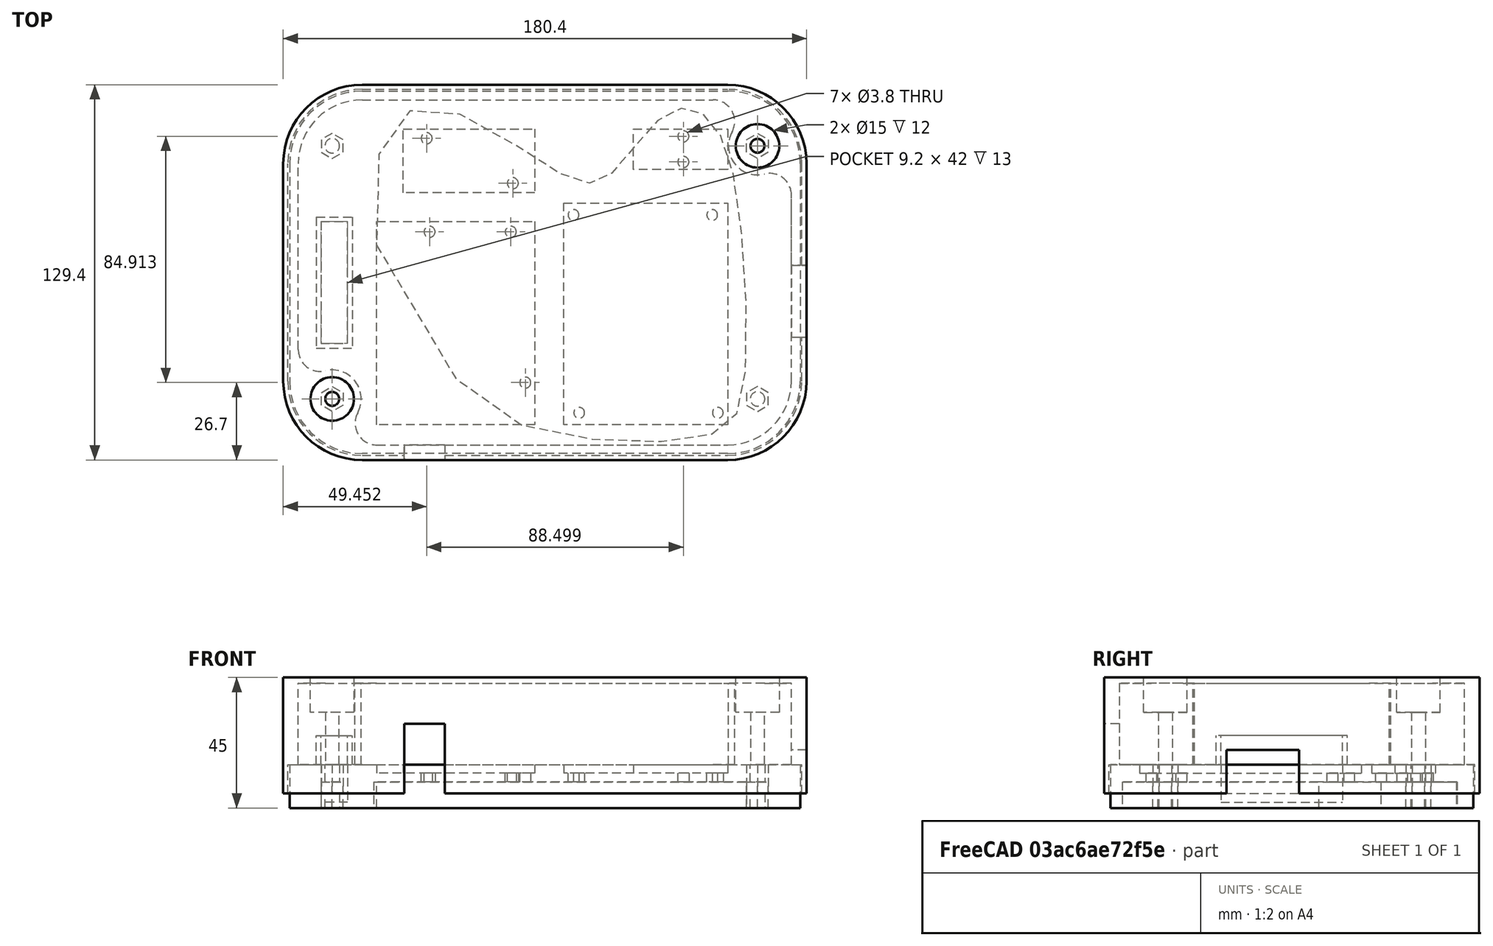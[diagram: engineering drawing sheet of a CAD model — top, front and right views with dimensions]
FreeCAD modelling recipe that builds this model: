
FCSTD DOCUMENT  (FreeCAD 0.21R33694 (Git))
Label: mers_door_controller
License: All rights reserved
LicenseURL: http://en.wikipedia.org/wiki/All_rights_reserved
objects: Sketcher::SketchObject×22, PartDesign::Pocket×17, PartDesign::Pad×5, PartDesign::Body×2, Mesh::Feature×2, PartDesign::Fillet×1, PartDesign::SubShapeBinder×1
note: 71 computed .brp shape members not serialized (recipe doc carries the construction recipe); baked Part::Feature solids carry a one-line shape summary decoded from their .brp

FEATURE [Sketcher::SketchObject] Sketch
  FullyConstrained = true
  MapMode = 5
  Support = -> [XY_Plane]
  sketch-geometry (4):
    g0: LineSegment StartX=-125 StartY=125 StartZ=0 EndX=125 EndY=125 EndZ=0
    g1: LineSegment StartX=125 StartY=125 StartZ=0 EndX=125 EndY=-125 EndZ=0
    g2: LineSegment StartX=125 StartY=-125 StartZ=0 EndX=-125 EndY=-125 EndZ=0
    g3: LineSegment StartX=-125 StartY=-125 StartZ=0 EndX=-125 EndY=125 EndZ=0
  constraints (11):
    c: Coincident(g0,g1)
    c: Coincident(g1,g2)
    c: Coincident(g2,g3)
    c: Coincident(g3,g0)
    c: Horizontal(g0)
    c: Horizontal(g2)
    c: Vertical(g1)
    c: Vertical(g3)
    c: Symmetric(g0,g2,g-1)
    c: Distance(g0) = 250
    c: Distance(g3) = 250
FEATURE [PartDesign::Pad] Pad
  Direction = (0,0,1)
  Length = 15
  Length2 = 10
  Profile = -> Sketch
  ReferenceAxis = -> Sketch [N_Axis]
  Type = 0
FEATURE [Sketcher::SketchObject] Sketch001
  ExternalGeometry = -> [Pad]
  FullyConstrained = true
  MapMode = 5
  Placement = pos=(0,0,15) rot=(0,0,1;0rad)
  Support = -> [Pad]
  sketch-geometry (16):
    g0: LineSegment StartX=-59.5 StartY=-45 StartZ=0 EndX=-5 EndY=-45 EndZ=0
    g1: LineSegment StartX=-5 StartY=-45 StartZ=0 EndX=-5 EndY=-115 EndZ=0
    g2: LineSegment StartX=-5 StartY=-115 StartZ=0 EndX=-59.5 EndY=-115 EndZ=0
    g3: LineSegment StartX=-59.5 StartY=-115 StartZ=0 EndX=-59.5 EndY=-45 EndZ=0
    g4: LineSegment StartX=5 StartY=-38.6 StartZ=0 EndX=61.5 EndY=-38.6 EndZ=0
    g5: LineSegment StartX=61.5 StartY=-38.6 StartZ=0 EndX=61.5 EndY=-115 EndZ=0
    g6: LineSegment StartX=61.5 StartY=-115 StartZ=0 EndX=5 EndY=-115 EndZ=0
    g7: LineSegment StartX=5 StartY=-115 StartZ=0 EndX=5 EndY=-38.6 EndZ=0
    g8: LineSegment StartX=-50.3 StartY=-13 StartZ=0 EndX=-5 EndY=-13 EndZ=0
    g9: LineSegment StartX=-5 StartY=-13 StartZ=0 EndX=-5 EndY=-35 EndZ=0
    g10: LineSegment StartX=-5 StartY=-35 StartZ=0 EndX=-50.3 EndY=-35 EndZ=0
    g11: LineSegment StartX=-50.3 StartY=-35 StartZ=0 EndX=-50.3 EndY=-13 EndZ=0
    g12: LineSegment StartX=29 StartY=-13 StartZ=0 EndX=61.5 EndY=-13 EndZ=0
    g13: LineSegment StartX=61.5 StartY=-13 StartZ=0 EndX=61.5 EndY=-27 EndZ=0
    g14: LineSegment StartX=61.5 StartY=-27 StartZ=0 EndX=29 EndY=-27 EndZ=0
    g15: LineSegment StartX=29 StartY=-27 StartZ=0 EndX=29 EndY=-13 EndZ=0
  constraints (47):
    c: Coincident(g0,g1)
    c: Coincident(g1,g2)
    c: Coincident(g2,g3)
    c: Coincident(g3,g0)
    c: Horizontal(g0)
    c: Horizontal(g2)
    c: Vertical(g1)
    c: Vertical(g3)
    c: Distance(g0) = 54.5
    c: Distance(g1) = 70
    c: Distance(g1,g-3) = 10
    c: Coincident(g4,g5)
    c: Coincident(g5,g6)
    c: Coincident(g6,g7)
    c: Coincident(g7,g4)
    c: Horizontal(g4)
    c: Horizontal(g6)
    c: Vertical(g5)
    c: Vertical(g7)
    c: Distance(g4) = 56.5
    c: Distance(g5) = 76.4
    c: DistanceX(g0,g4) = 10
    c: Coincident(g9,g10)
    c: Coincident(g10,g11)
    c: Coincident(g11,g8)
    c: Horizontal(g8)
    c: Horizontal(g10)
    c: Vertical(g9)
    c: Vertical(g11)
    c: Distance(g9) = 22
    c: Distance(g10) = 45.3
    c: PointOnObject(g9,g1)
    c: DistanceY(g0,g10) = 10
    c: Coincident(g12,g13)
    c: Coincident(g13,g14)
    c: Coincident(g14,g15)
    c: Coincident(g15,g12)
    c: Horizontal(g12)
    c: Horizontal(g14)
    c: Vertical(g13)
    c: Vertical(g15)
    c: Distance(g12) = 32.5
    c: Distance(g13) = 14
    c: PointOnObject(g13,g5)
    c: Coincident(g8,g9)
    c: PointOnObject(g12,g8)
    c: Symmetric(g1,g6,g-2)
FEATURE [PartDesign::Pocket] Pocket
  BaseFeature = -> Pad
  Direction = (0,0,-1)
  Length = 3
  Length2 = 5
  Profile = -> Sketch001
  ReferenceAxis = -> Sketch001 [N_Axis]
  Type = 0
FEATURE [Sketcher::SketchObject] Sketch002
  ExternalGeometry = -> [Pocket]
  FullyConstrained = true
  MapMode = 5
  Placement = pos=(0,0,12) rot=(0,0,1;0rad)
  Support = -> [Pocket]
  expr: Constraints[4] = 51 - 3.2
  expr: Constraints[5] = 71.45 - 3.2
  sketch-geometry (7):
    g0: Circle CenterX=8.37519 CenterY=-42.6889 CenterZ=0 NormalX=0 NormalY=0 NormalZ=1 AngleXU=0 Radius=1.85
    g1: Circle CenterX=56.1752 CenterY=-42.6889 CenterZ=0 NormalX=0 NormalY=0 NormalZ=1 AngleXU=0 Radius=1.85
    g2: Circle CenterX=58.1248 CenterY=-110.911 CenterZ=0 NormalX=0 NormalY=0 NormalZ=1 AngleXU=0 Radius=1.85
    g3: Circle CenterX=10.3248 CenterY=-110.911 CenterZ=0 NormalX=0 NormalY=0 NormalZ=1 AngleXU=0 Radius=1.85
    g4: LineSegment StartX=61.5 StartY=-38.6 StartZ=0 EndX=5 EndY=-115 EndZ=0
    g5: LineSegment StartX=5 StartY=-38.6 StartZ=0 EndX=61.5 EndY=-115 EndZ=0
    g6: GeomPoint X=33.25 Y=-76.8 Z=0
  constraints (16):
    c: Equal(g1,g0)
    c: Equal(g0,g3)
    c: Equal(g3,g2)
    c: Diameter(g1) = 3.7
    c: Distance(g0,g1) = 47.8
    c: Distance(g1,g2) = 68.25
    c: Coincident(g4,g-5)
    c: Coincident(g4,g-6)
    c: Tangent(g4,g1)
    c: Coincident(g5,g-4)
    c: Coincident(g5,g-6)
    c: PointOnObject(g6,g5)
    c: PointOnObject(g6,g4)
    c: Symmetric(g1,g3,g6)
    c: Symmetric(g0,g2,g6)
    c: Horizontal(g3,g2)
FEATURE [PartDesign::Pocket] Pocket001
  BaseFeature = -> Pocket
  Direction = (0,0,-1)
  Length = 5
  Length2 = 5
  Profile = -> Sketch002
  ReferenceAxis = -> Sketch002 [N_Axis]
  Type = 1
FEATURE [Sketcher::SketchObject] Sketch003
  ExternalGeometry = -> [Pocket001]
  FullyConstrained = true
  MapMode = 5
  Placement = pos=(0,0,12) rot=(0,0,1;0rad)
  Support = -> [Pocket001]
  expr: Constraints[21] = 1 + 3.8 / 2
  expr: Constraints[22] = 1 + 3.8 / 2
  expr: Constraints[23] = 12 + 3.8 / 2
  expr: Constraints[24] = 6 + 3.8 / 2
  expr: Constraints[3] = 31.8 - 3.8
  sketch-geometry (10):
    g0: Circle CenterX=-41.25 CenterY=-48.5 CenterZ=0 NormalX=0 NormalY=0 NormalZ=1 AngleXU=0 Radius=1.9
    g1: Circle CenterX=-13.25 CenterY=-48.5 CenterZ=0 NormalX=0 NormalY=0 NormalZ=1 AngleXU=0 Radius=1.9
    g2: Circle CenterX=-8.25 CenterY=-100.5 CenterZ=0 NormalX=0 NormalY=0 NormalZ=1 AngleXU=0 Radius=1.9
    g3: LineSegment StartX=-59.15 StartY=-45.6 StartZ=0 EndX=-5.35 EndY=-45.6 EndZ=0
    g4: LineSegment StartX=-5.35 StartY=-45.6 StartZ=0 EndX=-5.35 EndY=-114.4 EndZ=0
    g5: LineSegment StartX=-5.35 StartY=-114.4 StartZ=0 EndX=-59.15 EndY=-114.4 EndZ=0
    g6: LineSegment StartX=-59.15 StartY=-114.4 StartZ=0 EndX=-59.15 EndY=-45.6 EndZ=0
    g7: LineSegment StartX=-5 StartY=-45 StartZ=0 EndX=-59.5 EndY=-115 EndZ=0
    g8: LineSegment StartX=-5 StartY=-115 StartZ=0 EndX=-59.5 EndY=-45 EndZ=0
    g9: GeomPoint X=-32.25 Y=-80 Z=0
  constraints (25):
    c: Equal(g1,g2)
    c: Equal(g2,g0)
    c: Diameter(g0) = 3.8
    c: Distance(g0,g1) = 28
    c: Horizontal(g0,g1)
    c: Coincident(g3,g4)
    c: Coincident(g4,g5)
    c: Coincident(g5,g6)
    c: Coincident(g6,g3)
    c: Horizontal(g3)
    c: Vertical(g4)
    c: Coincident(g7,g-5)
    c: Coincident(g7,g-6)
    c: Coincident(g8,g-5)
    c: Coincident(g8,g-6)
    c: PointOnObject(g9,g7)
    c: PointOnObject(g9,g8)
    c: Symmetric(g5,g3,g9)
    c: Symmetric(g3,g4,g9)
    c: Distance(g5) = 53.8
    c: Distance(g6) = 68.8
    c: Distance(g1,g3) = 2.9
    c: Distance(g2,g4) = 2.9
    c: Distance(g2,g5) = 13.9
    c: Distance(g1,g4) = 7.9
FEATURE [PartDesign::Pocket] Pocket002
  BaseFeature = -> Pocket001
  Direction = (0,0,-1)
  Length = 5
  Length2 = 5
  Profile = -> Sketch003
  ReferenceAxis = -> Sketch003 [N_Axis]
  Type = 1
FEATURE [Sketcher::SketchObject] Sketch004
  ExternalGeometry = -> [Pocket002]
  FullyConstrained = true
  MapMode = 5
  Placement = pos=(0,0,12) rot=(0,0,1;0rad)
  Support = -> [Pocket002]
  expr: Constraints[19] = 37 - 3.5
  expr: Constraints[20] = 1 + 3.5 / 2
  expr: Constraints[21] = 5.3 + 3.5 / 2
  expr: Constraints[22] = 1 + 3.5 / 2
  sketch-geometry (9):
    g0: Circle CenterX=-42.2485 CenterY=-16.25 CenterZ=0 NormalX=0 NormalY=0 NormalZ=1 AngleXU=0 Radius=1.9
    g1: Circle CenterX=-12.55 CenterY=-31.75 CenterZ=0 NormalX=0 NormalY=0 NormalZ=1 AngleXU=0 Radius=1.9
    g2: LineSegment StartX=-50.3 StartY=-35 StartZ=0 EndX=-5 EndY=-13 EndZ=0
    g3: LineSegment StartX=-50.3 StartY=-13 StartZ=0 EndX=-5 EndY=-35 EndZ=0
    g4: GeomPoint X=-27.65 Y=-24 Z=0
    g5: LineSegment StartX=-49.8 StartY=-13.5 StartZ=0 EndX=-5.5 EndY=-13.5 EndZ=0
    g6: LineSegment StartX=-5.5 StartY=-13.5 StartZ=0 EndX=-5.5 EndY=-34.5 EndZ=0
    g7: LineSegment StartX=-5.5 StartY=-34.5 StartZ=0 EndX=-49.8 EndY=-34.5 EndZ=0
    g8: LineSegment StartX=-49.8 StartY=-34.5 StartZ=0 EndX=-49.8 EndY=-13.5 EndZ=0
  constraints (23):
    c: Equal(g1,g0)
    c: Diameter(g0) = 3.8
    c: Coincident(g2,g-6)
    c: Coincident(g2,g-4)
    c: Coincident(g3,g-6)
    c: Coincident(g3,g-5)
    c: PointOnObject(g4,g2)
    c: PointOnObject(g4,g3)
    c: Coincident(g5,g6)
    c: Coincident(g6,g7)
    c: Coincident(g7,g8)
    c: Coincident(g8,g5)
    c: Horizontal(g5)
    c: Horizontal(g7)
    c: Vertical(g6)
    c: Vertical(g8)
    c: Distance(g6) = 21
    c: Distance(g7) = 44.3
    c: Symmetric(g7,g5,g4)
    c: Distance(g0,g1) = 33.5
    c: Distance(g1,g7) = 2.75
    c: Distance(g1,g6) = 7.05
    c: Distance(g0,g5) = 2.75
FEATURE [PartDesign::Pocket] Pocket003
  BaseFeature = -> Pocket002
  Direction = (0,0,-1)
  Length = 5
  Length2 = 5
  Profile = -> Sketch004
  ReferenceAxis = -> Sketch004 [N_Axis]
  Type = 1
FEATURE [Sketcher::SketchObject] Sketch005
  ExternalGeometry = -> [Pocket003]
  FullyConstrained = true
  MapMode = 5
  Placement = pos=(0,0,12) rot=(0,0,1;0rad)
  Support = -> [Pocket003]
  expr: Constraints[21] = 13 + 3.5 / 2
  sketch-geometry (11):
    g0: LineSegment StartX=61.5 StartY=-13 StartZ=0 EndX=29 EndY=-27 EndZ=0
    g1: LineSegment StartX=29 StartY=-13 StartZ=0 EndX=61.5 EndY=-27 EndZ=0
    g2: GeomPoint X=45.25 Y=-20 Z=0
    g3: LineSegment StartX=29.5 StartY=-13.5 StartZ=0 EndX=61 EndY=-13.5 EndZ=0
    g4: LineSegment StartX=61 StartY=-13.5 StartZ=0 EndX=61 EndY=-26.5 EndZ=0
    g5: LineSegment StartX=61 StartY=-26.5 StartZ=0 EndX=29.5 EndY=-26.5 EndZ=0
    g6: LineSegment StartX=29.5 StartY=-26.5 StartZ=0 EndX=29.5 EndY=-13.5 EndZ=0
    g7: Circle CenterX=46.25 CenterY=-15.5869 CenterZ=0 NormalX=0 NormalY=0 NormalZ=1 AngleXU=0 Radius=1.9
    g8: Circle CenterX=46.25 CenterY=-24.4131 CenterZ=0 NormalX=0 NormalY=0 NormalZ=1 AngleXU=0 Radius=1.9
    g9: LineSegment StartX=46.25 StartY=-15.5869 StartZ=0 EndX=45.25 EndY=-20 EndZ=0
    g10: LineSegment StartX=46.25 StartY=-24.4131 StartZ=0 EndX=45.25 EndY=-20 EndZ=0
  constraints (27):
    c: Coincident(g0,g-6)
    c: Coincident(g0,g-5)
    c: Coincident(g1,g-5)
    c: Coincident(g1,g-6)
    c: PointOnObject(g2,g0)
    c: PointOnObject(g2,g1)
    c: Coincident(g3,g4)
    c: Coincident(g4,g5)
    c: Coincident(g5,g6)
    c: Coincident(g6,g3)
    c: Horizontal(g3)
    c: Horizontal(g5)
    c: Vertical(g4)
    c: Vertical(g6)
    c: Distance(g4) = 13
    c: Distance(g5) = 31.5
    c: Symmetric(g5,g3,g2)
    c: Equal(g8,g7)
    c: Diameter(g7) = 3.8
    c: Distance(g7,g8) = 8.82622
    c: Vertical(g7,g8)
    c: Distance(g8,g4) = 14.75
    c: Coincident(g9,g7)
    c: Coincident(g9,g2)
    c: Coincident(g10,g8)
    c: Coincident(g10,g2)
    c: Equal(g10,g9)
FEATURE [PartDesign::Pocket] Pocket004
  BaseFeature = -> Pocket003
  Direction = (0,0,-1)
  Length = 5
  Length2 = 5
  Profile = -> Sketch005
  ReferenceAxis = -> Sketch005 [N_Axis]
  Type = 1
FEATURE [Sketcher::SketchObject] Sketch006
  ExternalGeometry = -> [Pocket004]
  FullyConstrained = true
  MapMode = 5
  Placement = pos=(0,0,15) rot=(0,0,1;0rad)
  Support = -> [Pocket004]
  sketch-geometry (4):
    g0: LineSegment StartX=-78.7 StartY=-45 StartZ=0 EndX=-69.5 EndY=-45 EndZ=0
    g1: LineSegment StartX=-69.5 StartY=-45 StartZ=0 EndX=-69.5 EndY=-87 EndZ=0
    g2: LineSegment StartX=-69.5 StartY=-87 StartZ=0 EndX=-78.7 EndY=-87 EndZ=0
    g3: LineSegment StartX=-78.7 StartY=-87 StartZ=0 EndX=-78.7 EndY=-45 EndZ=0
  constraints (12):
    c: Coincident(g0,g1)
    c: Coincident(g1,g2)
    c: Coincident(g2,g3)
    c: Coincident(g3,g0)
    c: Horizontal(g0)
    c: Horizontal(g2)
    c: Vertical(g1)
    c: Vertical(g3)
    c: Distance(g0) = 9.2
    c: Distance(g1) = 42
    c: Distance(g0,g-3) = 10
    c: PointOnObject(g0,g-4)
FEATURE [PartDesign::Pocket] Pocket005
  BaseFeature = -> Pocket004
  Direction = (0,0,-1)
  Length = 13
  Length2 = 5
  Profile = -> Sketch006
  ReferenceAxis = -> Sketch006 [N_Axis]
  Type = 0
FEATURE [Sketcher::SketchObject] Sketch007
  ExternalGeometry = -> [Pocket005]
  FullyConstrained = true
  MapMode = 5
  Placement = pos=(0,0,15) rot=(0,0,1;0rad)
  Support = -> [Pocket005]
  sketch-geometry (11):
    g0: LineSegment StartX=-78.7 StartY=-45 StartZ=0 EndX=-78.7 EndY=-87 EndZ=0
    g1: LineSegment StartX=-69.5 StartY=-87 StartZ=0 EndX=-69.5 EndY=-45 EndZ=0
    g2: LineSegment StartX=-78.7 StartY=-87 StartZ=0 EndX=-69.5 EndY=-87 EndZ=0
    g3: LineSegment StartX=-78.7 StartY=-45 StartZ=0 EndX=-69.5 EndY=-45 EndZ=0
    g4: LineSegment StartX=-80.3 StartY=-43.4 StartZ=0 EndX=-67.9 EndY=-43.4 EndZ=0
    g5: LineSegment StartX=-67.9 StartY=-43.4 StartZ=0 EndX=-67.9 EndY=-88.6 EndZ=0
    g6: LineSegment StartX=-80.3 StartY=-88.6 StartZ=0 EndX=-67.9 EndY=-88.6 EndZ=0
    g7: LineSegment StartX=-80.3 StartY=-43.4 StartZ=0 EndX=-80.3 EndY=-88.6 EndZ=0
    g8: LineSegment StartX=-69.5 StartY=-45 StartZ=0 EndX=-78.7 EndY=-87 EndZ=0
    g9: LineSegment StartX=-78.7 StartY=-45 StartZ=0 EndX=-69.5 EndY=-87 EndZ=0
    g10: GeomPoint X=-74.1 Y=-66 Z=0
  constraints (24):
    c: Coincident(g3,g1)
    c: Coincident(g0,g3)
    c: Coincident(g0,g2)
    c: Coincident(g2,g1)
    c: Coincident(g1,g-6)
    c: Coincident(g0,g-6)
    c: Coincident(g-4,g1)
    c: Coincident(g0,g-5)
    c: Coincident(g4,g5)
    c: Coincident(g7,g4)
    c: Coincident(g7,g6)
    c: Coincident(g6,g5)
    c: Coincident(g8,g1)
    c: Coincident(g8,g0)
    c: Coincident(g9,g0)
    c: Coincident(g9,g1)
    c: PointOnObject(g10,g8)
    c: PointOnObject(g10,g9)
    c: Symmetric(g6,g4,g10)
    c: Symmetric(g5,g4,g10)
    c: Parallel(g1,g5)
    c: Parallel(g3,g4)
    c: Distance(g1,g5) = 1.6
    c: Distance(g1,g4) = 1.6
FEATURE [PartDesign::Pad] Pad001
  BaseFeature = -> Pocket005
  Direction = (0,0,1)
  Length = 10
  Length2 = 10
  Profile = -> Sketch007
  ReferenceAxis = -> Sketch007 [N_Axis]
  Type = 0
FEATURE [Sketcher::SketchObject] Sketch008
  ExternalGeometry = -> [Pad001]
  FullyConstrained = true
  MapMode = 5
  Placement = pos=(0,0,15) rot=(0,0,1;0rad)
  Support = -> [Pad001]
  sketch-geometry (12):
    g0: Circle CenterX=71.5 CenterY=-15 CenterZ=0 NormalX=0 NormalY=0 NormalZ=1 AngleXU=0 Radius=15
    g1: Circle CenterX=71.5 CenterY=-110 CenterZ=0 NormalX=0 NormalY=0 NormalZ=1 AngleXU=0 Radius=15
    g2: Circle CenterX=-74.5 CenterY=-15 CenterZ=0 NormalX=0 NormalY=0 NormalZ=1 AngleXU=0 Radius=15
    g3: Circle CenterX=-74.5 CenterY=-110 CenterZ=0 NormalX=0 NormalY=0 NormalZ=1 AngleXU=0 Radius=15
    g4: LineSegment StartX=-89.5 StartY=-125 StartZ=0 EndX=86.5 EndY=-125 EndZ=0
    g5: LineSegment StartX=86.5 StartY=0 StartZ=0 EndX=86.5 EndY=-125 EndZ=0
    g6: LineSegment StartX=-89.5 StartY=0 StartZ=0 EndX=86.5 EndY=0 EndZ=0
    g7: LineSegment StartX=-89.5 StartY=0 StartZ=0 EndX=-89.5 EndY=-125 EndZ=0
    g8: LineSegment StartX=-150 StartY=150 StartZ=0 EndX=150 EndY=150 EndZ=0
    g9: LineSegment StartX=150 StartY=150 StartZ=0 EndX=150 EndY=-150 EndZ=0
    g10: LineSegment StartX=150 StartY=-150 StartZ=0 EndX=-150 EndY=-150 EndZ=0
    g11: LineSegment StartX=-150 StartY=-150 StartZ=0 EndX=-150 EndY=150 EndZ=0
  constraints (35):
    c: Equal(g0,g1)
    c: Equal(g1,g3)
    c: Equal(g3,g2)
    c: Diameter(g2) = 30
    c: Tangent(g3,g-4)
    c: Tangent(g1,g-4)
    c: Tangent(g0,g-1)
    c: Tangent(g2,g-1)
    c: Vertical(g1,g0)
    c: Vertical(g2,g3)
    c: Distance(g1,g-6) = 10
    c: Tangent(g3,g-7)
    c: Coincident(g7,g6)
    c: Coincident(g6,g5)
    c: Coincident(g4,g5)
    c: Coincident(g4,g7)
    c: PointOnObject(g5,g-1)
    c: PointOnObject(g6,g-1)
    c: PointOnObject(g4,g-4)
    c: PointOnObject(g4,g-4)
    c: Tangent(g0,g5)
    c: Tangent(g1,g5)
    c: Tangent(g7,g3)
    c: Tangent(g2,g7)
    c: Coincident(g8,g9)
    c: Coincident(g9,g10)
    c: Coincident(g10,g11)
    c: Coincident(g11,g8)
    c: Horizontal(g8)
    c: Horizontal(g10)
    c: Vertical(g9)
    c: Vertical(g11)
    c: Symmetric(g10,g8,g-1)
    c: Distance(g9) = 300
    c: Distance(g8) = 300
FEATURE [PartDesign::Pocket] Pocket006
  BaseFeature = -> Pad001
  Direction = (0,0,-1)
  Length = 5
  Length2 = 5
  Profile = -> Sketch008
  ReferenceAxis = -> Sketch008 [N_Axis]
  Type = 1
FEATURE [PartDesign::Fillet] Fillet
  Base = -> Pocket006 [Edge18,Edge20,Edge17,Edge22]
  BaseFeature = -> Pocket006
  Radius = 25
  SupportTransform = false
  UseAllEdges = false
FEATURE [Sketcher::SketchObject] Sketch009
  ExternalGeometry = -> [Fillet]
  FullyConstrained = true
  MapMode = 5
  Placement = pos=(0,0,15) rot=(0,0,1;0rad)
  Support = -> [Fillet]
  sketch-geometry (7):
    g0: Circle CenterX=-74.8115 CenterY=-18.8622 CenterZ=0 NormalX=0 NormalY=0 NormalZ=1 AngleXU=0 Radius=2.5
    g1: Circle CenterX=-74.8115 CenterY=-106.138 CenterZ=0 NormalX=0 NormalY=0 NormalZ=1 AngleXU=0 Radius=2.5
    g2: Circle CenterX=71.8115 CenterY=-106.138 CenterZ=0 NormalX=0 NormalY=0 NormalZ=1 AngleXU=0 Radius=2.5
    g3: Circle CenterX=71.8115 CenterY=-18.8622 CenterZ=0 NormalX=0 NormalY=0 NormalZ=1 AngleXU=0 Radius=2.5
    g4: LineSegment StartX=-64.5 StartY=-100 StartZ=0 EndX=61.5 EndY=-25 EndZ=0
    g5: LineSegment StartX=61.5 StartY=-100 StartZ=0 EndX=-64.5 EndY=-25 EndZ=0
    g6: GeomPoint X=-1.5 Y=-62.5 Z=0
  constraints (16):
    c: Equal(g0,g3)
    c: Equal(g3,g2)
    c: Equal(g2,g1)
    c: Diameter(g0) = 5
    c: Coincident(g4,g-5)
    c: Coincident(g4,g-3)
    c: Coincident(g5,g-4)
    c: Coincident(g5,g-6)
    c: PointOnObject(g6,g5)
    c: PointOnObject(g6,g4)
    c: Symmetric(g2,g0,g6)
    c: Symmetric(g1,g3,g6)
    c: Distance(g4,g3) = 12
    c: Distance(g5,g2) = 12
    c: PointOnObject(g2,g5)
    c: PointOnObject(g1,g4)
FEATURE [PartDesign::Pocket] Pocket007
  BaseFeature = -> Fillet
  Direction = (0,0,-1)
  Length = 5
  Length2 = 5
  Profile = -> Sketch009
  ReferenceAxis = -> Sketch009 [N_Axis]
  Type = 1
FEATURE [Sketcher::SketchObject] Sketch010
  FullyConstrained = false
  MapMode = 5
  Placement = pos=(0,0,0) rot=(1,0,0;3.14159rad)
  Support = -> [Pocket007]
  sketch-geometry (25):
    g0-g12: Circle x13 (B-spline internal-alignment scaffolding for g13; pole/knot coordinates omitted)
    g13: BSplineCurve PolesCount=13 KnotsCount=11 Degree=3 IsPeriodic=0
    g14-g24: GeomPoint x11 (B-spline internal-alignment scaffolding for g13; pole/knot coordinates omitted)
  constraints (5):
    c: Weight(g0) = 1
    c: Equal(g0, g1-g12) x12
    c: Coincident(g13,g0)
    c: InternalAlignment(g0-g12 -> g13) x13
    c: InternalAlignment(g14-g24 -> g13) x11
FEATURE [PartDesign::Pocket] Pocket008
  BaseFeature = -> Pocket007
  Direction = (0,0,1)
  Length = 9
  Length2 = 5
  Profile = -> Sketch010
  ReferenceAxis = -> Sketch010 [N_Axis]
  Type = 0
FEATURE [Sketcher::SketchObject] Sketch011
  ExternalGeometry = -> [Pocket008]
  FullyConstrained = true
  MapMode = 5
  Placement = pos=(0,0,15) rot=(0,0,1;0rad)
  Support = -> [Pocket008]
  sketch-geometry (14):
    g0: LineSegment StartX=-71.0615 StartY=-21.0273 StartZ=0 EndX=-71.0615 EndY=-16.6971 EndZ=0
    g1: LineSegment StartX=-71.0615 StartY=-16.6971 StartZ=0 EndX=-74.8115 EndY=-14.5321 EndZ=0
    g2: LineSegment StartX=-74.8115 StartY=-14.5321 StartZ=0 EndX=-78.5615 EndY=-16.6971 EndZ=0
    g3: LineSegment StartX=-78.5615 StartY=-16.6971 StartZ=0 EndX=-78.5615 EndY=-21.0273 EndZ=0
    g4: LineSegment StartX=-78.5615 StartY=-21.0273 StartZ=0 EndX=-74.8115 EndY=-23.1923 EndZ=0
    g5: LineSegment StartX=-74.8115 StartY=-23.1923 StartZ=0 EndX=-71.0615 EndY=-21.0273 EndZ=0
    g6: Circle CenterX=-74.8115 CenterY=-18.8622 CenterZ=0 NormalX=0 NormalY=0 NormalZ=1 AngleXU=0 Radius=4.33013
    g7: LineSegment StartX=75.5615 StartY=-108.303 StartZ=0 EndX=75.5615 EndY=-103.973 EndZ=0
    g8: LineSegment StartX=75.5615 StartY=-103.973 StartZ=0 EndX=71.8115 EndY=-101.808 EndZ=0
    g9: LineSegment StartX=71.8115 StartY=-101.808 StartZ=0 EndX=68.0615 EndY=-103.973 EndZ=0
    g10: LineSegment StartX=68.0615 StartY=-103.973 StartZ=0 EndX=68.0615 EndY=-108.303 EndZ=0
    g11: LineSegment StartX=68.0615 StartY=-108.303 StartZ=0 EndX=71.8115 EndY=-110.468 EndZ=0
    g12: LineSegment StartX=71.8115 StartY=-110.468 StartZ=0 EndX=75.5615 EndY=-108.303 EndZ=0
    g13: Circle CenterX=71.8115 CenterY=-106.138 CenterZ=0 NormalX=0 NormalY=0 NormalZ=1 AngleXU=0 Radius=4.33013
  constraints (32):
    c: Coincident(g0,g1)
    c: Coincident(g1,g2)
    c: Coincident(g2,g3)
    c: Coincident(g3,g4)
    c: Coincident(g4,g5)
    c: Coincident(g5,g0)
    c: Equal(g0, g1-g5) x5
    c: PointOnObject(g0,g6)
    c: PointOnObject(g1,g6)
    c: PointOnObject(g2,g6)
    c: PointOnObject(g3,g6)
    c: PointOnObject(g4,g6)
    c: PointOnObject(g5,g6)
    c: Coincident(g7,g8)
    c: Coincident(g8,g9)
    c: Coincident(g9,g10)
    c: Coincident(g10,g11)
    c: Coincident(g11,g12)
    c: Coincident(g12,g7)
    c: Equal(g7, g8-g12) x5
    c: PointOnObject(g7,g13)
    c: PointOnObject(g8,g13)
    c: PointOnObject(g9,g13)
    c: PointOnObject(g10,g13)
    c: PointOnObject(g11,g13)
    c: PointOnObject(g12,g13)
    c: Equal(g13,g6)
    c: Distance(g4,g0) = 7.5
    c: Coincident(g6,g-3)
    c: Coincident(g-4,g13)
    c: Vertical(g7)
    c: Vertical(g0)
FEATURE [PartDesign::Pocket] Pocket009
  BaseFeature = -> Pocket008
  Direction = (0,0,-1)
  Length = 10
  Length2 = 5
  Profile = -> Sketch011
  ReferenceAxis = -> Sketch011 [N_Axis]
  Type = 0
FEATURE [Sketcher::SketchObject] Sketch012
  ExternalGeometry = -> [Pocket009]
  FullyConstrained = true
  MapMode = 5
  Placement = pos=(0,0,0) rot=(1,0,0;3.14159rad)
  Support = -> [Pocket009]
  sketch-geometry (14):
    g0: LineSegment StartX=-71.0615 StartY=103.973 StartZ=0 EndX=-71.0615 EndY=108.303 EndZ=0
    g1: LineSegment StartX=-71.0615 StartY=108.303 StartZ=0 EndX=-74.8115 EndY=110.468 EndZ=0
    g2: LineSegment StartX=-74.8115 StartY=110.468 StartZ=0 EndX=-78.5615 EndY=108.303 EndZ=0
    g3: LineSegment StartX=-78.5615 StartY=108.303 StartZ=0 EndX=-78.5615 EndY=103.973 EndZ=0
    g4: LineSegment StartX=-78.5615 StartY=103.973 StartZ=0 EndX=-74.8115 EndY=101.808 EndZ=0
    g5: LineSegment StartX=-74.8115 StartY=101.808 StartZ=0 EndX=-71.0615 EndY=103.973 EndZ=0
    g6: Circle CenterX=-74.8115 CenterY=106.138 CenterZ=0 NormalX=0 NormalY=0 NormalZ=1 AngleXU=0 Radius=4.33013
    g7: LineSegment StartX=75.5615 StartY=16.6971 StartZ=0 EndX=75.5615 EndY=21.0273 EndZ=0
    g8: LineSegment StartX=75.5615 StartY=21.0273 StartZ=0 EndX=71.8115 EndY=23.1923 EndZ=0
    g9: LineSegment StartX=71.8115 StartY=23.1923 StartZ=0 EndX=68.0615 EndY=21.0273 EndZ=0
    g10: LineSegment StartX=68.0615 StartY=21.0273 StartZ=0 EndX=68.0615 EndY=16.6971 EndZ=0
    g11: LineSegment StartX=68.0615 StartY=16.6971 StartZ=0 EndX=71.8115 EndY=14.5321 EndZ=0
    g12: LineSegment StartX=71.8115 StartY=14.5321 StartZ=0 EndX=75.5615 EndY=16.6971 EndZ=0
    g13: Circle CenterX=71.8115 CenterY=18.8622 CenterZ=0 NormalX=0 NormalY=0 NormalZ=1 AngleXU=0 Radius=4.33013
  constraints (32):
    c: Coincident(g0,g1)
    c: Coincident(g1,g2)
    c: Coincident(g2,g3)
    c: Coincident(g3,g4)
    c: Coincident(g4,g5)
    c: Coincident(g5,g0)
    c: Equal(g0, g1-g5) x5
    c: PointOnObject(g0,g6)
    c: PointOnObject(g1,g6)
    c: PointOnObject(g2,g6)
    c: PointOnObject(g3,g6)
    c: PointOnObject(g4,g6)
    c: PointOnObject(g5,g6)
    c: Coincident(g7,g8)
    c: Coincident(g8,g9)
    c: Coincident(g9,g10)
    c: Coincident(g10,g11)
    c: Coincident(g11,g12)
    c: Coincident(g12,g7)
    c: Equal(g7, g8-g12) x5
    c: PointOnObject(g7,g13)
    c: PointOnObject(g8,g13)
    c: PointOnObject(g9,g13)
    c: PointOnObject(g10,g13)
    c: PointOnObject(g11,g13)
    c: PointOnObject(g12,g13)
    c: Equal(g13,g6)
    c: Distance(g11,g7) = 7.5
    c: Coincident(g-4,g13)
    c: Coincident(g-3,g6)
    c: Vertical(g0)
    c: Vertical(g7)
FEATURE [PartDesign::Pocket] Pocket010
  BaseFeature = -> Pocket009
  Direction = (0,0,1)
  Length = 9
  Length2 = 5
  Profile = -> Sketch012
  ReferenceAxis = -> Sketch012 [N_Axis]
  Type = 0
FEATURE [PartDesign::Body] Body
  Group = -> [Sketch,Pad,Sketch001,Pocket,Sketch002,Pocket001,Sketch003,Pocket002,Sketch004,Pocket003,Sketch005,Pocket004,Sketch006,Pocket005,Sketch007,Pad001,Sketch008,Pocket006,Fillet,Sketch009,Pocket007,Sketch010,Pocket008,Sketch011,Pocket009,Sketch012,Pocket010]
  Origin = -> Origin
  Tip = -> Pocket010
FEATURE [Mesh::Feature] Mesh  label="mercedes_door_controller"
FEATURE [PartDesign::SubShapeBinder] Binder
  BindCopyOnChange = 0
  BindMode = 0
  ClaimChildren = false
  Context = -> Body001 [Binder.]
  Fuse = false
  MakeFace = true
  OffsetFill = false
  OffsetIntersection = false
  OffsetJoinType = 0
  OffsetOpenResult = false
  PartialLoad = false
  Relative = true
  Support = -> [Body]
  _Version = 2
FEATURE [Sketcher::SketchObject] Sketch013
  ExternalGeometry = -> [Binder]
  FullyConstrained = true
  MapMode = 5
  Placement = pos=(0,0,15) rot=(0,0,1;0rad)
  Support = -> [Binder]
  sketch-geometry (8):
    g0: LineSegment StartX=-64.5 StartY=2.2 StartZ=0 EndX=61.5 EndY=2.2 EndZ=0
    g1: LineSegment StartX=88.7 StartY=-25 StartZ=0 EndX=88.7 EndY=-100 EndZ=0
    g2: LineSegment StartX=-64.5 StartY=-127.2 StartZ=0 EndX=61.5 EndY=-127.2 EndZ=0
    g3: LineSegment StartX=-91.7 StartY=-25 StartZ=0 EndX=-91.7 EndY=-100 EndZ=0
    g4: ArcOfCircle CenterX=-64.5 CenterY=-100 CenterZ=0 NormalX=0 NormalY=0 NormalZ=1 AngleXU=0 Radius=27.2 StartAngle=3.14159 EndAngle=4.71239
    g5: ArcOfCircle CenterX=-64.5 CenterY=-25 CenterZ=0 NormalX=0 NormalY=0 NormalZ=1 AngleXU=0 Radius=27.2 StartAngle=1.5708 EndAngle=3.14159
    g6: ArcOfCircle CenterX=61.5 CenterY=-25 CenterZ=0 NormalX=0 NormalY=0 NormalZ=1 AngleXU=0 Radius=27.2 StartAngle=1e-16 EndAngle=1.5708
    g7: ArcOfCircle CenterX=61.5 CenterY=-100 CenterZ=0 NormalX=0 NormalY=0 NormalZ=1 AngleXU=0 Radius=27.2 StartAngle=4.71239 EndAngle=6.28319
  constraints (16):
    c: Coincident(g5,g-7)
    c: Coincident(g-10,g4)
    c: Coincident(g-9,g7)
    c: Coincident(g6,g-8)
    c: Tangent(g5,g3) = -1.5708
    c: Tangent(g3,g4) = -1.5708
    c: Tangent(g4,g2) = -1.5708
    c: Tangent(g2,g7) = -1.5708
    c: Tangent(g7,g1) = 1.5708
    c: Tangent(g1,g6) = 1.5708
    c: Tangent(g0,g6) = 1.5708
    c: Tangent(g5,g0) = 1.5708
    c: Parallel(g3,g-5)
    c: Parallel(g-3,g1)
    c: Parallel(g-6,g0)
    c: Distance(g3,g-5) = 2.2
FEATURE [PartDesign::Pad] Pad002
  Direction = (0,0,1)
  Length = 30
  Length2 = 10
  Profile = -> Sketch013
  ReferenceAxis = -> Sketch013 [N_Axis]
  Type = 0
FEATURE [Sketcher::SketchObject] Sketch014
  ExternalGeometry = -> [Pad002]
  FullyConstrained = true
  MapMode = 5
  Placement = pos=(0,0,15) rot=(1,0,0;3.14159rad)
  Support = -> [Pad002]
  sketch-geometry (8):
    g0: LineSegment StartX=-64.5 StartY=127.2 StartZ=0 EndX=61.5 EndY=127.2 EndZ=0
    g1: LineSegment StartX=88.7 StartY=25 StartZ=0 EndX=88.7 EndY=100 EndZ=0
    g2: LineSegment StartX=-64.5 StartY=-2.2 StartZ=0 EndX=61.5 EndY=-2.2 EndZ=0
    g3: LineSegment StartX=-91.7 StartY=100 StartZ=0 EndX=-91.7 EndY=25 EndZ=0
    g4: ArcOfCircle CenterX=-64.5 CenterY=100 CenterZ=0 NormalX=0 NormalY=0 NormalZ=1 AngleXU=0 Radius=27.2 StartAngle=1.5708 EndAngle=3.14159
    g5: ArcOfCircle CenterX=-64.5 CenterY=25 CenterZ=0 NormalX=0 NormalY=0 NormalZ=1 AngleXU=0 Radius=27.2 StartAngle=3.14159 EndAngle=4.71239
    g6: ArcOfCircle CenterX=61.5 CenterY=25 CenterZ=0 NormalX=0 NormalY=0 NormalZ=1 AngleXU=0 Radius=27.2 StartAngle=4.71239 EndAngle=6.28319
    g7: ArcOfCircle CenterX=61.5 CenterY=100 CenterZ=0 NormalX=0 NormalY=0 NormalZ=1 AngleXU=0 Radius=27.2 StartAngle=0 EndAngle=1.5708
  constraints (15):
    c: Tangent(g4,g3) = -1.5708
    c: Tangent(g5,g3) = -1.5708
    c: Tangent(g5,g2) = -1.5708
    c: Tangent(g2,g6) = -1.5708
    c: Tangent(g6,g1) = -1.5708
    c: Tangent(g1,g7) = -1.5708
    c: Tangent(g0,g7) = 1.5708
    c: Tangent(g4,g0) = 1.5708
    c: Coincident(g4,g-10)
    c: Coincident(g7,g-4)
    c: Coincident(g6,g-6)
    c: Coincident(g-8,g5)
    c: Parallel(g1,g-5)
    c: Parallel(g3,g-9)
    c: Coincident(g-8,g2)
FEATURE [PartDesign::Pad] Pad003
  BaseFeature = -> Pad002
  Direction = (0,0,-1)
  Length = 10
  Length2 = 10
  Profile = -> Sketch014
  ReferenceAxis = -> Sketch014 [N_Axis]
  Type = 0
FEATURE [Sketcher::SketchObject] Sketch015
  ExternalGeometry = -> [Pad003]
  FullyConstrained = true
  MapMode = 5
  Placement = pos=(0,0,5) rot=(1,0,0;3.14159rad)
  Support = -> [Pad003]
  sketch-geometry (8):
    g0: LineSegment StartX=-64.5 StartY=125.6 StartZ=0 EndX=61.5 EndY=125.6 EndZ=0
    g1: LineSegment StartX=87.1 StartY=100 StartZ=0 EndX=87.1 EndY=25 EndZ=0
    g2: LineSegment StartX=-64.5 StartY=-0.6 StartZ=0 EndX=61.5 EndY=-0.6 EndZ=0
    g3: LineSegment StartX=-90.1 StartY=100 StartZ=0 EndX=-90.1 EndY=25 EndZ=0
    g4: ArcOfCircle CenterX=-64.5 CenterY=100 CenterZ=0 NormalX=0 NormalY=0 NormalZ=1 AngleXU=0 Radius=25.6 StartAngle=1.5708 EndAngle=3.14159
    g5: ArcOfCircle CenterX=61.5 CenterY=100 CenterZ=0 NormalX=0 NormalY=0 NormalZ=1 AngleXU=0 Radius=25.6 StartAngle=-9e-16 EndAngle=1.5708
    g6: ArcOfCircle CenterX=61.5 CenterY=25 CenterZ=0 NormalX=0 NormalY=0 NormalZ=1 AngleXU=0 Radius=25.6 StartAngle=4.71239 EndAngle=6.28319
    g7: ArcOfCircle CenterX=-64.5 CenterY=25 CenterZ=0 NormalX=0 NormalY=0 NormalZ=1 AngleXU=0 Radius=25.6 StartAngle=3.14159 EndAngle=4.71239
  constraints (16):
    c: Coincident(g4,g-8)
    c: Coincident(g-9,g5)
    c: Coincident(g-10,g6)
    c: Coincident(g-7,g7)
    c: Tangent(g4,g0) = 1.5708
    c: Tangent(g0,g5) = 1.5708
    c: Tangent(g1,g5) = 1.5708
    c: Tangent(g1,g6) = 1.5708
    c: Tangent(g2,g6) = -1.5708
    c: Tangent(g2,g7) = -1.5708
    c: Tangent(g7,g3) = -1.5708
    c: Tangent(g4,g3) = -1.5708
    c: Parallel(g-3,g1)
    c: Parallel(g-4,g0)
    c: Parallel(g3,g-5)
    c: Distance(g1,g-3) = 1.6
FEATURE [PartDesign::Pocket] Pocket011
  BaseFeature = -> Pad003
  Direction = (0,0,1)
  Length = 10
  Length2 = 5
  Profile = -> Sketch015
  ReferenceAxis = -> Sketch015 [N_Axis]
  Type = 0
FEATURE [Sketcher::SketchObject] Sketch016
  ExternalGeometry = -> [Binder]
  FullyConstrained = true
  MapMode = 5
  Placement = pos=(0,0,15) rot=(1,0,0;3.14159rad)
  Support = -> [Pocket011]
  sketch-geometry (8):
    g0: LineSegment StartX=-64.5 StartY=122 StartZ=0 EndX=61.5 EndY=122 EndZ=0
    g1: LineSegment StartX=83.5 StartY=100 StartZ=0 EndX=83.5 EndY=25 EndZ=0
    g2: LineSegment StartX=-64.5 StartY=3 StartZ=0 EndX=61.5 EndY=3 EndZ=0
    g3: LineSegment StartX=-86.5 StartY=100 StartZ=0 EndX=-86.5 EndY=25 EndZ=0
    g4: ArcOfCircle CenterX=-64.5 CenterY=100 CenterZ=0 NormalX=0 NormalY=0 NormalZ=1 AngleXU=0 Radius=22 StartAngle=1.5708 EndAngle=3.14159
    g5: ArcOfCircle CenterX=61.5 CenterY=100 CenterZ=0 NormalX=0 NormalY=0 NormalZ=1 AngleXU=0 Radius=22 StartAngle=1e-16 EndAngle=1.5708
    g6: ArcOfCircle CenterX=61.5 CenterY=25 CenterZ=0 NormalX=0 NormalY=0 NormalZ=1 AngleXU=0 Radius=22 StartAngle=4.71239 EndAngle=6.28319
    g7: ArcOfCircle CenterX=-64.5 CenterY=25 CenterZ=0 NormalX=0 NormalY=0 NormalZ=1 AngleXU=0 Radius=22 StartAngle=3.14159 EndAngle=4.71239
  constraints (16):
    c: Coincident(g-8,g7)
    c: Coincident(g-10,g4)
    c: Coincident(g5,g-4)
    c: Coincident(g-6,g6)
    c: Tangent(g4,g0) = 1.5708
    c: Tangent(g0,g5) = 1.5708
    c: Tangent(g5,g1) = 1.5708
    c: Tangent(g1,g6) = 1.5708
    c: Tangent(g2,g6) = -1.5708
    c: Tangent(g7,g2) = -1.5708
    c: Tangent(g3,g7) = -1.5708
    c: Tangent(g4,g3) = -1.5708
    c: Parallel(g-3,g0)
    c: Parallel(g-9,g3)
    c: Parallel(g1,g-5)
    c: Distance(g-6,g1) = 3
FEATURE [PartDesign::Pocket] Pocket012
  BaseFeature = -> Pocket011
  Direction = (0,0,1)
  Length = 28
  Length2 = 5
  Profile = -> Sketch016
  ReferenceAxis = -> Sketch016 [N_Axis]
  Type = 0
FEATURE [Sketcher::SketchObject] Sketch017
  ExternalGeometry = -> [Binder,Pocket012]
  FullyConstrained = true
  MapMode = 5
  Placement = pos=(0,0,43) rot=(1,0,0;3.14159rad)
  Support = -> [Pocket012]
  sketch-geometry (14):
    g0: Circle CenterX=-74.8115 CenterY=106.138 CenterZ=0 NormalX=0 NormalY=0 NormalZ=1 AngleXU=0 Radius=10
    g1: Circle CenterX=71.8115 CenterY=18.8622 CenterZ=0 NormalX=0 NormalY=0 NormalZ=1 AngleXU=0 Radius=10
    g2: ArcOfCircle CenterX=-64.5 CenterY=100 CenterZ=0 NormalX=0 NormalY=0 NormalZ=1 AngleXU=0 Radius=22 StartAngle=1.5708 EndAngle=3.14159
    g3: ArcOfCircle CenterX=61.5 CenterY=25 CenterZ=0 NormalX=0 NormalY=0 NormalZ=1 AngleXU=0 Radius=22 StartAngle=4.71239 EndAngle=6.28319
    g4: ArcOfCircle CenterX=-74.8115 CenterY=106.138 CenterZ=0 NormalX=0 NormalY=0 NormalZ=1 AngleXU=0 Radius=10 StartAngle=4.4707 EndAngle=6.78138
    g5: ArcOfCircle CenterX=71.8115 CenterY=18.8622 CenterZ=0 NormalX=0 NormalY=0 NormalZ=1 AngleXU=0 Radius=10 StartAngle=1.32911 EndAngle=3.63979
    g6: LineSegment StartX=-64.5 StartY=122 StartZ=0 EndX=-59.4387 EndY=122 EndZ=0
    g7: LineSegment StartX=-86.5 StartY=100 StartZ=0 EndX=-86.5 EndY=89.1464 EndZ=0
    g8: ArcOfCircle CenterX=-79 CenterY=89.1464 CenterZ=0 NormalX=0 NormalY=0 NormalZ=1 AngleXU=0 Radius=7.5 StartAngle=1.32911 EndAngle=3.14159
    g9: ArcOfCircle CenterX=-59.4387 CenterY=114.5 CenterZ=0 NormalX=0 NormalY=0 NormalZ=1 AngleXU=0 Radius=7.5 StartAngle=1.5708 EndAngle=3.63979
    g10: LineSegment StartX=83.5 StartY=35.8536 StartZ=0 EndX=83.5 EndY=25 EndZ=0
    g11: LineSegment StartX=56.4387 StartY=3 StartZ=0 EndX=61.5 EndY=3 EndZ=0
    g12: ArcOfCircle CenterX=76 CenterY=35.8536 CenterZ=0 NormalX=0 NormalY=0 NormalZ=1 AngleXU=0 Radius=7.5 StartAngle=4.4707 EndAngle=6.28319
    g13: ArcOfCircle CenterX=56.4387 CenterY=10.5 CenterZ=0 NormalX=0 NormalY=0 NormalZ=1 AngleXU=0 Radius=7.5 StartAngle=4.71239 EndAngle=6.78138
  constraints (32):
    c: Coincident(g0,g-3)
    c: Coincident(g1,g-4)
    c: Tangent(g0,g-10)
    c: Tangent(g1,g-6)
    c: Coincident(g2,g-10)
    c: Coincident(g-6,g3)
    c: Coincident(g5,g1)
    c: Tangent(g2,g6) = 1.5708
    c: Tangent(g2,g7) = -1.5708
    c: Tangent(g7,g8) = -1.5708
    c: Tangent(g4,g8) = 1.5708
    c: Tangent(g4,g9) = 1.5708
    c: Tangent(g6,g9) = 1.5708
    c: Tangent(g13,g5) = 1.5708
    c: Tangent(g5,g12) = 1.5708
    c: Tangent(g13,g11) = -1.5708
    c: Tangent(g11,g3) = -1.5708
    c: Tangent(g10,g3) = 1.5708
    c: Tangent(g12,g10) = 1.5708
    c: Tangent(g4,g0) = -1.5708
    c: Equal(g0,g4)
    c: Equal(g5,g1)
    c: PointOnObject(g7,g-11)
    c: PointOnObject(g11,g-5)
    c: PointOnObject(g10,g-7)
    c: PointOnObject(g6,g-9)
    c: Equal(g-10,g2)
    c: Equal(g-6,g3)
    c: Equal(g12,g13)
    c: Diameter(g12) = 15
    c: Equal(g9,g8)
    c: Diameter(g9) = 15
FEATURE [PartDesign::Pad] Pad004
  BaseFeature = -> Pocket012
  Direction = (0,0,-1)
  Length = 10
  Length2 = 10
  Profile = -> Sketch017
  ReferenceAxis = -> Sketch017 [N_Axis]
  Type = 3
  UpToFace = -> Pocket012 [Face27]
FEATURE [Sketcher::SketchObject] Sketch018
  ExternalGeometry = -> [Pad004]
  FullyConstrained = true
  MapMode = 5
  Placement = pos=(0,0,15) rot=(1,0,0;3.14159rad)
  Support = -> [Pad004]
  sketch-geometry (2):
    g0: Circle CenterX=-74.8115 CenterY=106.138 CenterZ=0 NormalX=0 NormalY=0 NormalZ=1 AngleXU=0 Radius=2.4
    g1: Circle CenterX=71.8115 CenterY=18.8622 CenterZ=0 NormalX=0 NormalY=0 NormalZ=1 AngleXU=0 Radius=2.4
  constraints (4):
    c: Equal(g0,g1)
    c: Coincident(g0,g-3)
    c: Coincident(g1,g-4)
    c: Diameter(g0) = 4.8
FEATURE [PartDesign::Pocket] Pocket013
  BaseFeature = -> Pad004
  Direction = (0,0,1)
  Length = 5
  Length2 = 5
  Profile = -> Sketch018
  ReferenceAxis = -> Sketch018 [N_Axis]
  Type = 1
FEATURE [Sketcher::SketchObject] Sketch019
  ExternalGeometry = -> [Pocket013]
  FullyConstrained = true
  MapMode = 5
  Placement = pos=(0,0,45) rot=(0,0,1;0rad)
  Support = -> [Pocket013]
  sketch-geometry (2):
    g0: Circle CenterX=71.8115 CenterY=-18.8622 CenterZ=0 NormalX=0 NormalY=0 NormalZ=1 AngleXU=0 Radius=7.5
    g1: Circle CenterX=-74.8115 CenterY=-106.138 CenterZ=0 NormalX=0 NormalY=0 NormalZ=1 AngleXU=0 Radius=7.5
  constraints (4):
    c: Coincident(g0,g-3)
    c: Coincident(g-4,g1)
    c: Equal(g1,g0)
    c: Diameter(g0) = 15
FEATURE [PartDesign::Pocket] Pocket014
  BaseFeature = -> Pocket013
  Direction = (0,0,-1)
  Length = 12
  Length2 = 5
  Profile = -> Sketch019
  ReferenceAxis = -> Sketch019 [N_Axis]
  Type = 0
FEATURE [Sketcher::SketchObject] Sketch020
  ExternalGeometry = -> [Binder]
  FullyConstrained = true
  MapMode = 5
  Placement = pos=(0,-122,0) rot=(0,0.707107,0.707107;3.14159rad)
  Support = -> [Pocket014]
  sketch-geometry (4):
    g0: LineSegment StartX=36 StartY=29 StartZ=0 EndX=50 EndY=29 EndZ=0
    g1: LineSegment StartX=50 StartY=29 StartZ=0 EndX=50 EndY=-11 EndZ=0
    g2: LineSegment StartX=50 StartY=-11 StartZ=0 EndX=36 EndY=-11 EndZ=0
    g3: LineSegment StartX=36 StartY=-11 StartZ=0 EndX=36 EndY=29 EndZ=0
  constraints (12):
    c: Coincident(g0,g1)
    c: Coincident(g1,g2)
    c: Coincident(g2,g3)
    c: Coincident(g3,g0)
    c: Horizontal(g0)
    c: Horizontal(g2)
    c: Vertical(g1)
    c: Vertical(g3)
    c: Distance(g0) = 14
    c: Distance(g-4,g1) = 9.5
    c: Distance(g0,g-4) = 14
    c: Distance(g3) = 40
FEATURE [PartDesign::Pocket] Pocket015
  BaseFeature = -> Pocket014
  Direction = (0,-1,2e-16)
  Length = 5
  Length2 = 5
  Profile = -> Sketch020
  ReferenceAxis = -> Sketch020 [N_Axis]
  Type = 1
FEATURE [Sketcher::SketchObject] Sketch021
  ExternalGeometry = -> [Pocket015]
  FullyConstrained = true
  MapMode = 5
  Placement = pos=(88.7,1.68e-14,0) rot=(0.57735,0.57735,0.57735;2.0944rad)
  Support = -> [Pocket015]
  sketch-geometry (4):
    g0: LineSegment StartX=-85 StartY=20 StartZ=0 EndX=-60 EndY=20 EndZ=0
    g1: LineSegment StartX=-60 StartY=20 StartZ=0 EndX=-60 EndY=-10 EndZ=0
    g2: LineSegment StartX=-60 StartY=-10 StartZ=0 EndX=-85 EndY=-10 EndZ=0
    g3: LineSegment StartX=-85 StartY=-10 StartZ=0 EndX=-85 EndY=20 EndZ=0
  constraints (12):
    c: Coincident(g0,g1)
    c: Coincident(g1,g2)
    c: Coincident(g2,g3)
    c: Coincident(g3,g0)
    c: Horizontal(g0)
    c: Horizontal(g2)
    c: Vertical(g1)
    c: Vertical(g3)
    c: Distance(g0) = 25
    c: Distance(g0,g-3) = 5
    c: Distance(g-3,g3) = 15
    c: Distance(g1) = 30
FEATURE [PartDesign::Pocket] Pocket016
  BaseFeature = -> Pocket015
  Direction = (-1,-1e-16,-1e-16)
  Length = 10
  Length2 = 5
  Profile = -> Sketch021
  ReferenceAxis = -> Sketch021 [N_Axis]
  Type = 0
FEATURE [PartDesign::Body] Body001
  Group = -> [Binder,Sketch013,Pad002,Sketch014,Pad003,Sketch015,Pocket011,Sketch016,Pocket012,Sketch017,Pad004,Sketch018,Pocket013,Sketch019,Pocket014,Sketch020,Pocket015,Sketch021,Pocket016]
  Origin = -> Origin001
  Tip = -> Pocket016
FEATURE [Mesh::Feature] Mesh001  label="mercedes_door_controller_cover"
